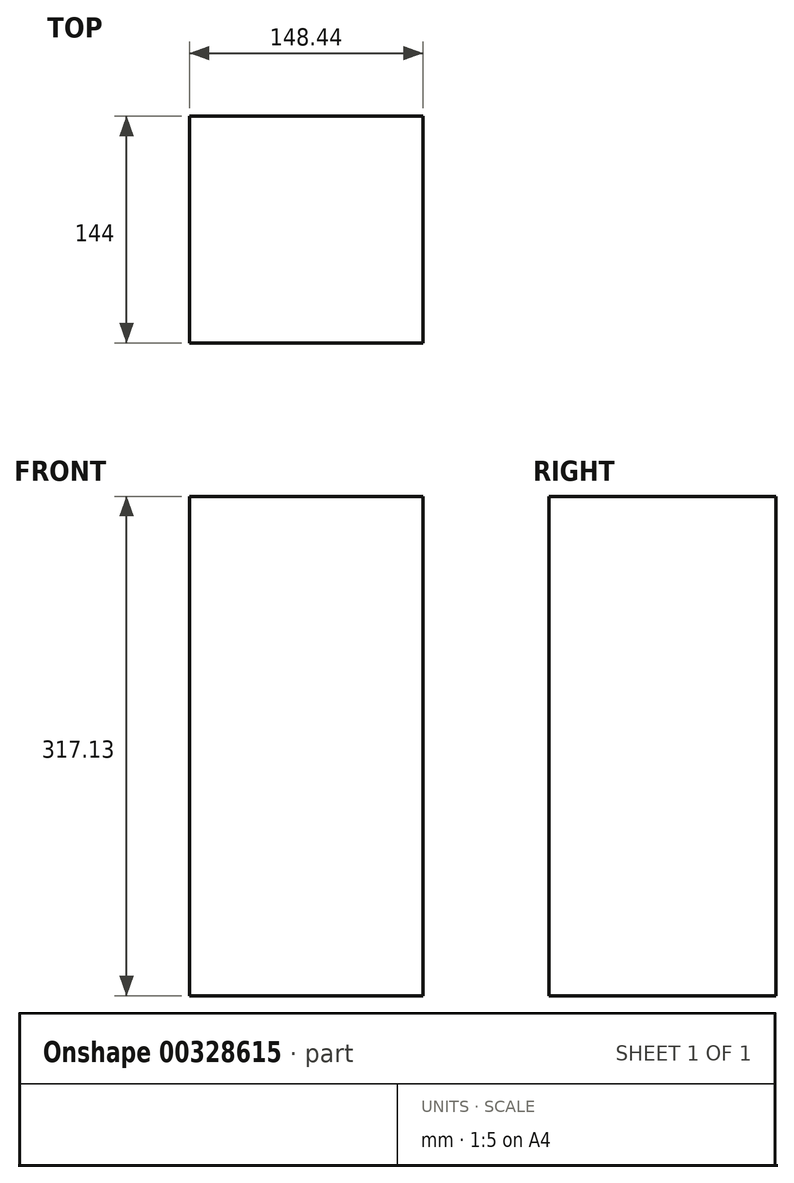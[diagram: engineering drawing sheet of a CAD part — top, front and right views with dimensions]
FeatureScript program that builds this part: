
annotation { "Feature Type Name" : "Feature", "Feature Type Description" : "" }
export const myFeature = defineFeature(function(context is Context, id is Id, definition is map)
    precondition{}
    {
        {
            var Q0;
            Q0=qCreatedBy(makeId("Front.planeOp"),FACE);
            var sketch = newSketch(context, id + "F0", { "sketchPlane" : qUnion([Q0])});
            skLineSegment(sketch, "E0.bottom", {"start": v(68.03, 0) * mm, "end": v(216.47, 0) * mm});
            skLineSegment(sketch, "E0.top", {"start": v(68.03, -317.13) * mm, "end": v(216.47, -317.13) * mm});
            skLineSegment(sketch, "E0.left", {"start": v(68.03, 0) * mm, "end": v(68.03, -317.13) * mm});
            skLineSegment(sketch, "E0.right", {"start": v(216.47, 0) * mm, "end": v(216.47, -317.13) * mm});
            skSolve(sketch);
        }
        {
            var Q0;
            Q0=makeQuery(id+"F0.imprint","IMPRINT",FACE,{"disambiguationData":[TD([[makeQuery(id+"F0.imprint","IMPRINT",EDGE,{"derivedFrom":sQuery(id+"F0.wireOp",EDGE,"E0.bottom")}),-1.0]])]});
            extrude(context, id + "F1", {"entities" : qUnion([Q0]), "depth" : 144 * mm});
        }
    });
